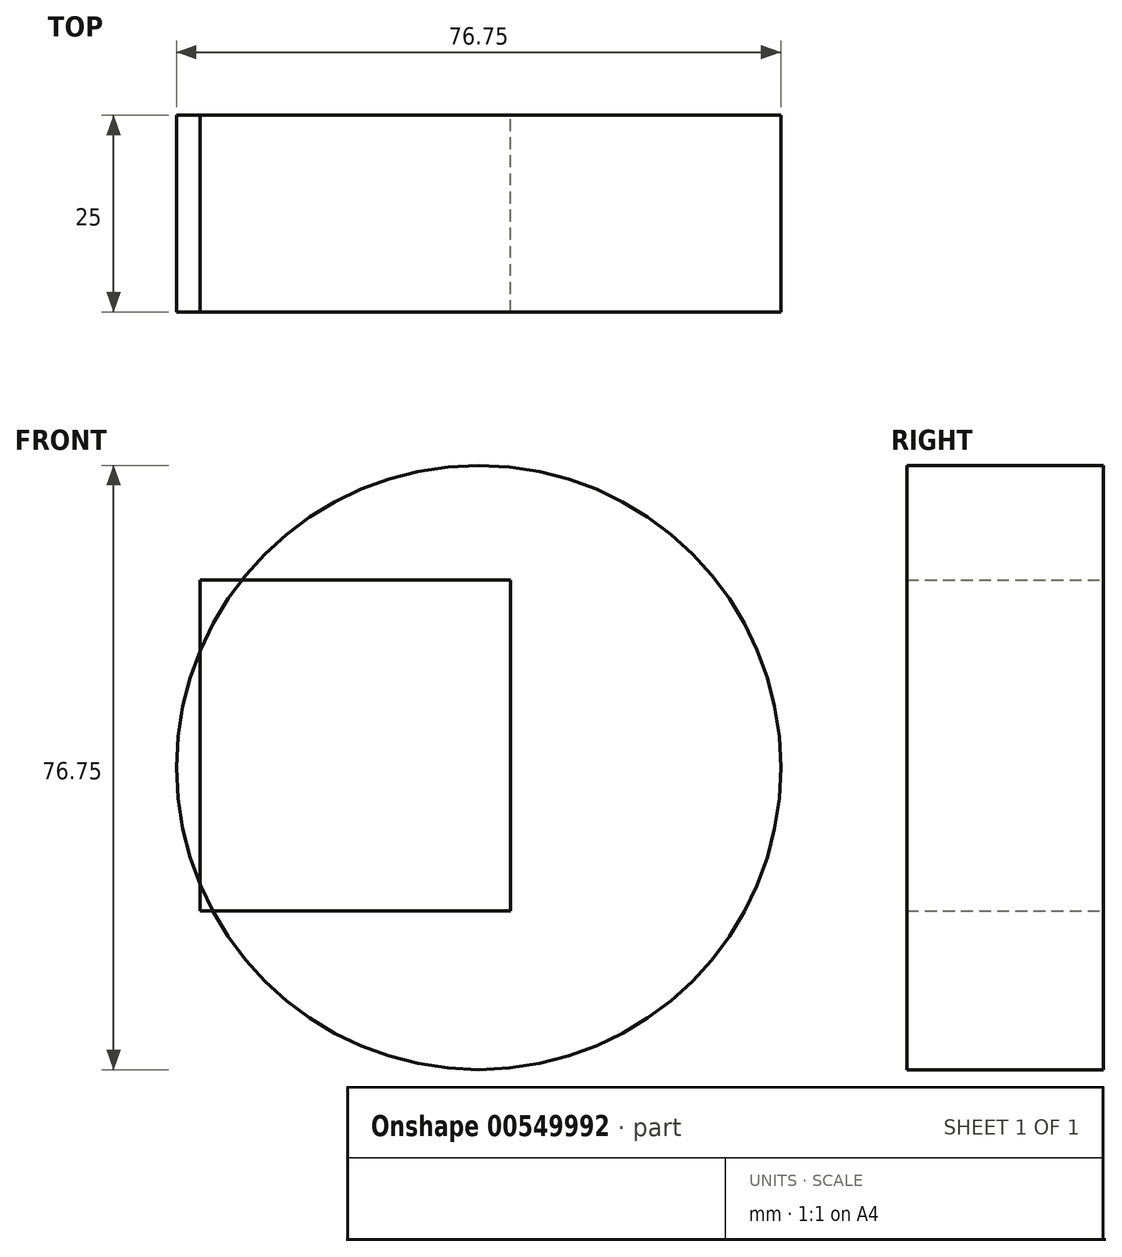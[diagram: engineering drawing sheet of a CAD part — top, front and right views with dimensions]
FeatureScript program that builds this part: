
annotation { "Feature Type Name" : "Feature", "Feature Type Description" : "" }
export const myFeature = defineFeature(function(context is Context, id is Id, definition is map)
    precondition{}
    {
        {
            var Q0;
            Q0=qCreatedBy(makeId("Front.planeOp"),FACE);
            var sketch = newSketch(context, id + "F0", { "sketchPlane" : qUnion([Q0])});
            skLineSegment(sketch, "E0.bottom", {"start": v(-92.13, 16.13) * mm, "end": v(-52.74, 16.13) * mm});
            skLineSegment(sketch, "E0.top", {"start": v(-92.13, 58.2) * mm, "end": v(-52.74, 58.2) * mm});
            skLineSegment(sketch, "E0.left", {"start": v(-92.13, 16.13) * mm, "end": v(-92.13, 58.2) * mm});
            skLineSegment(sketch, "E0.right", {"start": v(-52.74, 16.13) * mm, "end": v(-52.74, 58.2) * mm});
            skPoint(sketch, "E0.middle", {"position": v(-72.43, 37.17) * mm});
            skSolve(sketch);
        }
        {
            var Q0;
            Q0 = qSketchRegion(id + "F0", true);
            extrude(context, id + "F1", {"entities" : qUnion([Q0]), "depth" : 25 * mm, "offsetDistance" : 25 * mm});
        }
        {
            var Q0;
            Q0=qCreatedBy(makeId("Front.planeOp"),FACE);
            var sketch = newSketch(context, id + "F2", { "sketchPlane" : qUnion([Q0])});
            skCircle(sketch, "E1", {"center": v(-56.74, 34.36) * mm, "radius": 38.38 * mm});
            skSolve(sketch);
        }
        {
            var Q0;
            Q0 = qSketchRegion(id + "F2", true);
            extrude(context, id + "F3", {"entities" : qUnion([Q0]), "depth" : 25 * mm, "offsetDistance" : 25 * mm});
        }
    });
